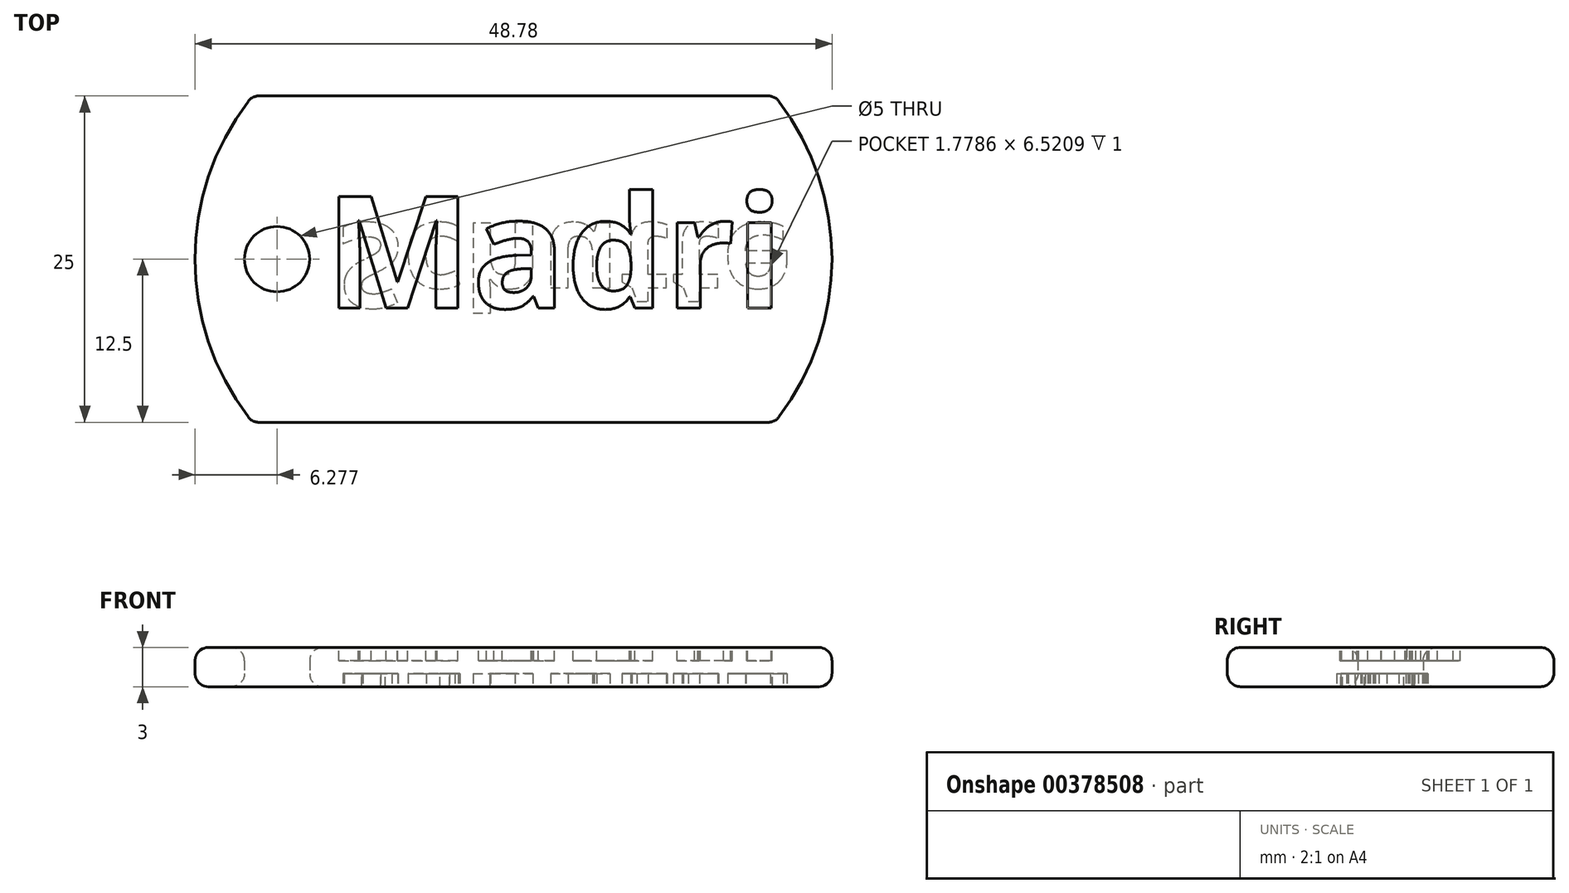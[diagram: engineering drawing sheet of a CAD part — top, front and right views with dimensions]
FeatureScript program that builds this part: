
annotation { "Feature Type Name" : "Feature", "Feature Type Description" : "" }
export const myFeature = defineFeature(function(context is Context, id is Id, definition is map)
    precondition{}
    {
        {
            var Q0;
            Q0=qCreatedBy(makeId("Top.planeOp"),FACE);
            var sketch = newSketch(context, id + "F0", { "sketchPlane" : qUnion([Q0])});
            skLineSegment(sketch, "E0.bottom", {"start": v(-20, 12.5) * mm, "end": v(20, 12.5) * mm});
            skLineSegment(sketch, "E0.top", {"start": v(-20, -12.5) * mm, "end": v(20, -12.5) * mm});
            skArc(sketch, "E1", {"start": v(-20, 12.5) * mm, "mid": v(-24.39, 0) * mm, "end": v(-20, -12.5) * mm});
            skArc(sketch, "E2", {"start": v(20, -12.5) * mm, "mid": v(24.39, 0) * mm, "end": v(20, 12.5) * mm});
            skCircle(sketch, "E3", {"center": v(-18.11, 0) * mm, "radius": 2.5 * mm});
            skSolve(sketch);
        }
        {
            var Q0;
            Q0=makeQuery(id+"F0.imprint","IMPRINT",FACE,{"disambiguationData":[TD([[makeQuery(id+"F0.imprint","IMPRINT",EDGE,{"derivedFrom":sQuery(id+"F0.wireOp",EDGE,"E0.bottom")}),-1.0]])]});
            extrude(context, id + "F1", {"entities" : qUnion([Q0]), "depth" : 3 * mm});
        }
        {
            var Q0;
            Q0=makeQuery(id+"F1.opExtrude","CAP_FACE",FACE,{"disambiguationData":[OSD([sQuery(id+"F0.wireOp",EDGE,"E0.bottom"),sQuery(id+"F0.wireOp",EDGE,"E0.top"),sQuery(id+"F0.wireOp",EDGE,"E1"),sQuery(id+"F0.wireOp",EDGE,"E2"),sQuery(id+"F0.wireOp",EDGE,"E3")])],"isStart":false});
            var sketch = newSketch(context, id + "F2", { "sketchPlane" : qUnion([Q0])});
            skText(sketch, "E4", { "text": "Madri\n", "fontName": "OpenSans-Bold.ttf"});
            const initialGuessF2  = {"E4": [-0.01445, -0.00374, 1, 0, 0.0086]};
            skSetInitialGuess(sketch, initialGuessF2);
            skSolve(sketch);
        }
        {
            var Q0;
            Q0=qSketchRegion(id+"F2",true);
            extrude(context, id + "F3", {"entities" : qUnion([Q0]), "operationType" : NewBodyOperationType.REMOVE, "oppositeDirection" : true, "depth" : 1 * mm});
        }
        {
            var Q0;
            Q0=makeQuery(id+"F1.opExtrude","CAP_FACE",FACE,{"disambiguationData":[OSD([sQuery(id+"F0.wireOp",EDGE,"E0.bottom"),sQuery(id+"F0.wireOp",EDGE,"E0.top"),sQuery(id+"F0.wireOp",EDGE,"E1"),sQuery(id+"F0.wireOp",EDGE,"E2"),sQuery(id+"F0.wireOp",EDGE,"E3")])],"isStart":true});
            var sketch = newSketch(context, id + "F4", { "sketchPlane" : qUnion([Q0])});
            skText(sketch, "E5", { "text": "Schutte", "fontName": "OpenSans-Bold.ttf"});
            const initialGuessF4  = {"E5": [-0.01347, -0.00276, 1, 0, 0.00653]};
            skSetInitialGuess(sketch, initialGuessF4);
            skSolve(sketch);
        }
        {
            var Q0;
            Q0=qSketchRegion(id+"F4",true);
            extrude(context, id + "F5", {"entities" : qUnion([Q0]), "operationType" : NewBodyOperationType.REMOVE, "oppositeDirection" : true, "depth" : 1 * mm});
        }
        {
            var Q0;
            Q0=makeQuery(id+"F1.opExtrude","SWEPT_FACE",FACE,{"disambiguationData":[OSD([sQuery(id+"F0.wireOp",EDGE,"E0.top")])]});
            var Q1;
            Q1=makeQuery(id+"F1.opExtrude","SWEPT_FACE",FACE,{"disambiguationData":[OSD([sQuery(id+"F0.wireOp",EDGE,"E2")])]});
            var Q2;
            Q2=makeQuery(id+"F1.opExtrude","SWEPT_FACE",FACE,{"disambiguationData":[OSD([sQuery(id+"F0.wireOp",EDGE,"E1")])]});
            var Q3;
            Q3=makeQuery(id+"F1.opExtrude","SWEPT_FACE",FACE,{"disambiguationData":[OSD([sQuery(id+"F0.wireOp",EDGE,"E0.bottom")])]});
            var Q4;
            Q4=makeQuery(id+"F1.opExtrude","CAP_EDGE",EDGE,{"disambiguationData":[OSD([sQuery(id+"F0.wireOp",EDGE,"E3")])],"isStart":true});
            var Q5;
            Q5=makeQuery(id+"F1.opExtrude","SWEPT_FACE",FACE,{"disambiguationData":[OSD([sQuery(id+"F0.wireOp",EDGE,"E3")])]});
            fillet(context, id + "F6", {"entities" : qUnion([Q0, Q1, Q2, Q3, Q4, Q5]), "radius" : 1 * mm, "tangentPropagation" : true, "allowEdgeOverflow" : false});
        }
    });
